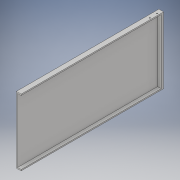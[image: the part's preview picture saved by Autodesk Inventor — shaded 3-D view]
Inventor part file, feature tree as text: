
AUTODESK INVENTOR PART (.ipt)
format: ipt  version: 2017 (Build 210142000, 142)  size: 128,000 bytes
history: native  units: in
note: dims shown in document units (in); Inventor stores cm internally (conversion verified against a paired STEP export)
features: extrude x3, sketch x2, hole x1
ambient origin geometry x8: Origin, YZ Plane, XZ Plane, XY Plane, X Axis, Y Axis, Z Axis, Center Point
bodies: Solid1 (feature_tree)
feature tree (6):
  sketch  "Sketch1"  dims[d0=7.0in d1=15.0in]
  extrude  "Extrusion1"  Depth=15.0in
  extrude  "Extrusion2"  Depth=15.0in
  extrude  "Extrusion3"  TaperAngle=0.0deg  [1 undecoded]
  hole  "Hole1"  [1 undecoded]
  sketch  "Sketch2"  dims[d2=6.75in d3=15.0in d4=0.0in d5=0.125in d6=0.125in d7=0.0in d8=0.5in d9=0.0in d10=0.25in d11=0.5in d12=0.0in d13=14.5in d14=90.0deg d15=0.77in d16=0.1875in d17=0.125in d18=0.75in d19=0.375in d20=0.25in d21=0.5635in d22=1.0in d23=0.8108in]
note: 2 required parameter values undecoded (feature->parameter linkage not recoverable at this tier; creation-order binding heuristic only, values carry confidence <= 0.55)
